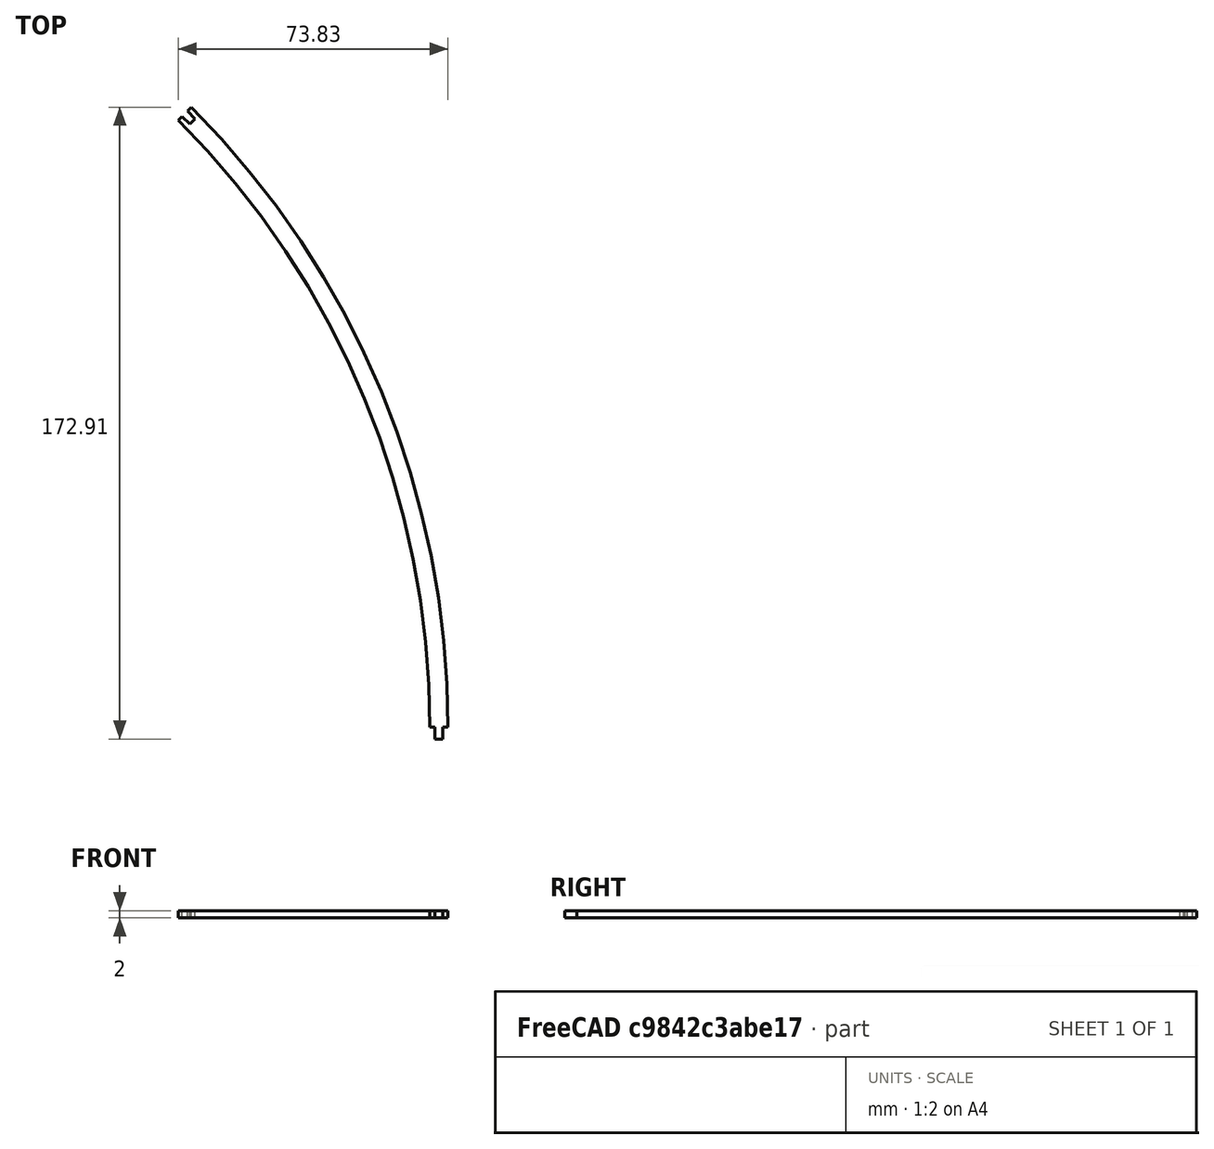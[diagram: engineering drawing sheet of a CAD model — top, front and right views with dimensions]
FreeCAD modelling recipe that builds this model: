
FCSTD DOCUMENT  (FreeCAD 1.0R39109 (Git))
Label: squirrel baffle reinforcement
License: All rights reserved
LicenseURL: https://en.wikipedia.org/wiki/All_rights_reserved
objects: Sketcher::SketchObject×1, PartDesign::Pad×1, PartDesign::Body×1
note: 6 computed .brp shape members not serialized (recipe doc carries the construction recipe); baked Part::Feature solids carry a one-line shape summary decoded from their .brp

FEATURE [Sketcher::SketchObject] Sketch
  ArcFitTolerance = 1e-06
  AttachmentSupport = -> [XY_Plane]
  FullyConstrained = true
  MakeInternals = false
  MapMode = 5
  sketch-geometry (13):
    g0: ArcOfCircle CenterX=0 CenterY=0 CenterZ=0 NormalX=0 NormalY=0 NormalZ=1 AngleXU=0 Radius=235 StartAngle=0 EndAngle=0.785398
    g1: ArcOfCircle CenterX=0 CenterY=0 CenterZ=0 NormalX=0 NormalY=0 NormalZ=1 AngleXU=0 Radius=240 StartAngle=0 EndAngle=0.785398
    g2: LineSegment [constr] StartX=0 StartY=0 StartZ=0 EndX=166.17 EndY=166.17 EndZ=0
    g3: LineSegment StartX=169.706 StartY=169.706 StartZ=0 EndX=168.645 EndY=168.645 EndZ=0
    g4: LineSegment StartX=168.645 StartY=168.645 StartZ=0 EndX=170.766 EndY=166.524 EndZ=0
    g5: LineSegment StartX=170.766 StartY=166.524 StartZ=0 EndX=169.352 EndY=165.109 EndZ=0
    g6: LineSegment StartX=169.352 StartY=165.109 StartZ=0 EndX=167.231 EndY=167.231 EndZ=0
    g7: LineSegment StartX=167.231 StartY=167.231 StartZ=0 EndX=166.17 EndY=166.17 EndZ=0
    g8: LineSegment StartX=235 StartY=0 StartZ=0 EndX=236.4 EndY=0 EndZ=0
    g9: LineSegment StartX=240 StartY=0 StartZ=0 EndX=238.6 EndY=0 EndZ=0
    g10: LineSegment StartX=236.4 StartY=0 StartZ=0 EndX=236.4 EndY=-3.2 EndZ=0
    g11: LineSegment StartX=236.4 StartY=-3.2 StartZ=0 EndX=238.6 EndY=-3.2 EndZ=0
    g12: LineSegment StartX=238.6 StartY=-3.2 StartZ=0 EndX=238.6 EndY=0 EndZ=0
  constraints (38):
    c: Coincident(g0,g-1)
    c: Coincident(g1,g0)
    c: Diameter(g0) = 470
    c: Diameter(g1) = 480
    c: PointOnObject(g1,g-1)
    c: PointOnObject(g0,g-1)
    c: Coincident(g2,g0)
    c: Coincident(g2,g0)
    c: Angle(g-1,g2) = 0.785398
    c: Coincident(g3,g1)
    c: Coincident(g4,g3)
    c: Coincident(g5,g4)
    c: Coincident(g7,g0)
    c: Equal(g7,g3)
    c: Coincident(g7,g6)
    c: Coincident(g5,g6)
    c: Perpendicular(g6,g7)
    c: Perpendicular(g5,g6)
    c: Perpendicular(g4,g5)
    c: Perpendicular(g3,g4)
    c: Perpendicular(g0,g7)
    c: Perpendicular(g1,g3)
    c: Distance(g6) = 3
    c: Distance(g5) = 2
    c: Coincident(g8,g0)
    c: PointOnObject(g8,g-1)
    c: Coincident(g9,g1)
    c: PointOnObject(g9,g-1)
    c: Coincident(g8,g10)
    c: Coincident(g10,g11)
    c: Coincident(g11,g12)
    c: Coincident(g12,g9)
    c: Vertical(g12)
    c: Vertical(g10)
    c: Horizontal(g11)
    c: Equal(g8,g9)
    c: DistanceX(g11,g11) = 2.2
    c: DistanceY(g10,g10) = 3.2
FEATURE [PartDesign::Pad] Pad
  Direction = (0,0,1)
  Length = 2
  Length2 = 10
  Profile = -> Sketch
  ReferenceAxis = -> Sketch [N_Axis]
  Refine = true
  Suppressed = false
  Type = 0
FEATURE [PartDesign::Body] Body
  AllowCompound = false
  Group = -> [Sketch,Pad]
  Origin = -> Origin
  Tip = -> Pad
